# Revit family: Faucet-Power_Supply-KOHLER-K-16306T
name_source: partatom
category: Specialty Equipment
units: mm (PartAtom-declared; Revit-internal decimal feet)

## family parameters
Cut with Voids When Loaded = No
Host = Face
OmniClass Number = 23.31.25.00
OmniClass Title = Toilet and Bath Specialties
Part Type = Normal
Room Calculation Point = No
Round Connector Dimension = Use Diameter
Shared = No

## types (1)
- NA-Not Applicable
    ADA Compliant = No
    Apparent Load = 0 VA
    Assembly Code = C1030200
    Date Modified = 09/14/2023
    Default Elevation = 42"
    Description = POWER SUPPLY, 3V
    Electrical Connector = Yes
    Finish = Kohler-Plastic-0-White
    Height = 4 1/8"
    Length = 2 3/16"
    Manufacturer = Kohler Co.
    Master Format 2014 = 10 28 00
    Master Format 2014 Name = Toilet, Bath, and Laundry Accessories
    Material = Plastic Construction
    Model = K-16306T-NA
    Type = 1
    URL = http://www.kohler.com.cn
    Voltage = 3 V
    WaterSense Certified = No
    Width = 1 1/16"

## geometry (parser evidence)
native form markers: Sweep x5
no freeform markers — native parametric forms only
